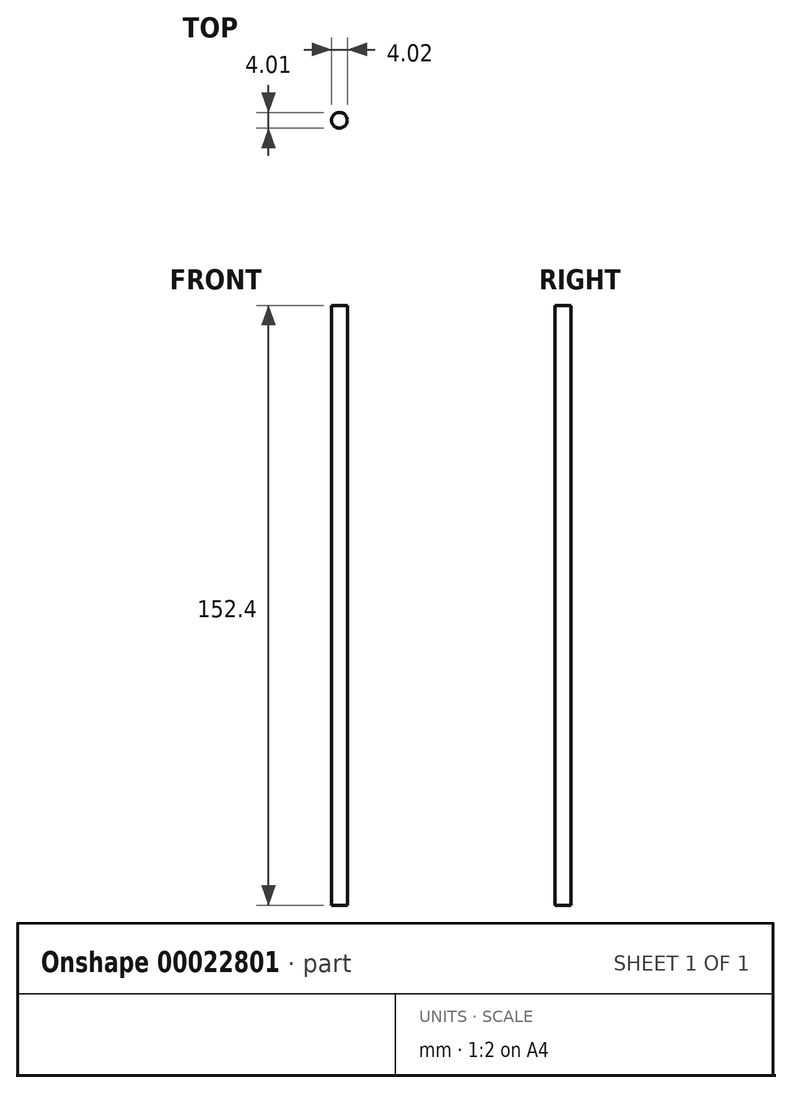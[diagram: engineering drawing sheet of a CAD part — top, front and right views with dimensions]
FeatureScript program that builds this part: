
annotation { "Feature Type Name" : "Feature", "Feature Type Description" : "" }
export const myFeature = defineFeature(function(context is Context, id is Id, definition is map)
    precondition{}
    {
        {
            var Q0;
            Q0=qCreatedBy(makeId("Top.planeOp"),FACE);
            var sketch = newSketch(context, id + "F0", { "sketchPlane" : qUnion([Q0])});
            skCircle(sketch, "E0", {"center": v(-27, 24.02) * mm, "radius": 2 * mm});
            skLineSegment(sketch, "E1", {"start": v(-27, 24.02) * mm, "end": v(-25, 24.02) * mm});
            skSolve(sketch);
        }
        {
            var Q0;
            Q0=makeQuery(id+"F0.imprint","IMPRINT",FACE,{"disambiguationData":[TD([[makeQuery(id+"F0.imprint","IMPRINT",EDGE,{"derivedFrom":sQuery(id+"F0.wireOp",EDGE,"E0")}),1.0]])]});
            extrude(context, id + "F1", {"entities" : qUnion([Q0]), "depth" : 152.4 * mm});
        }
    });
